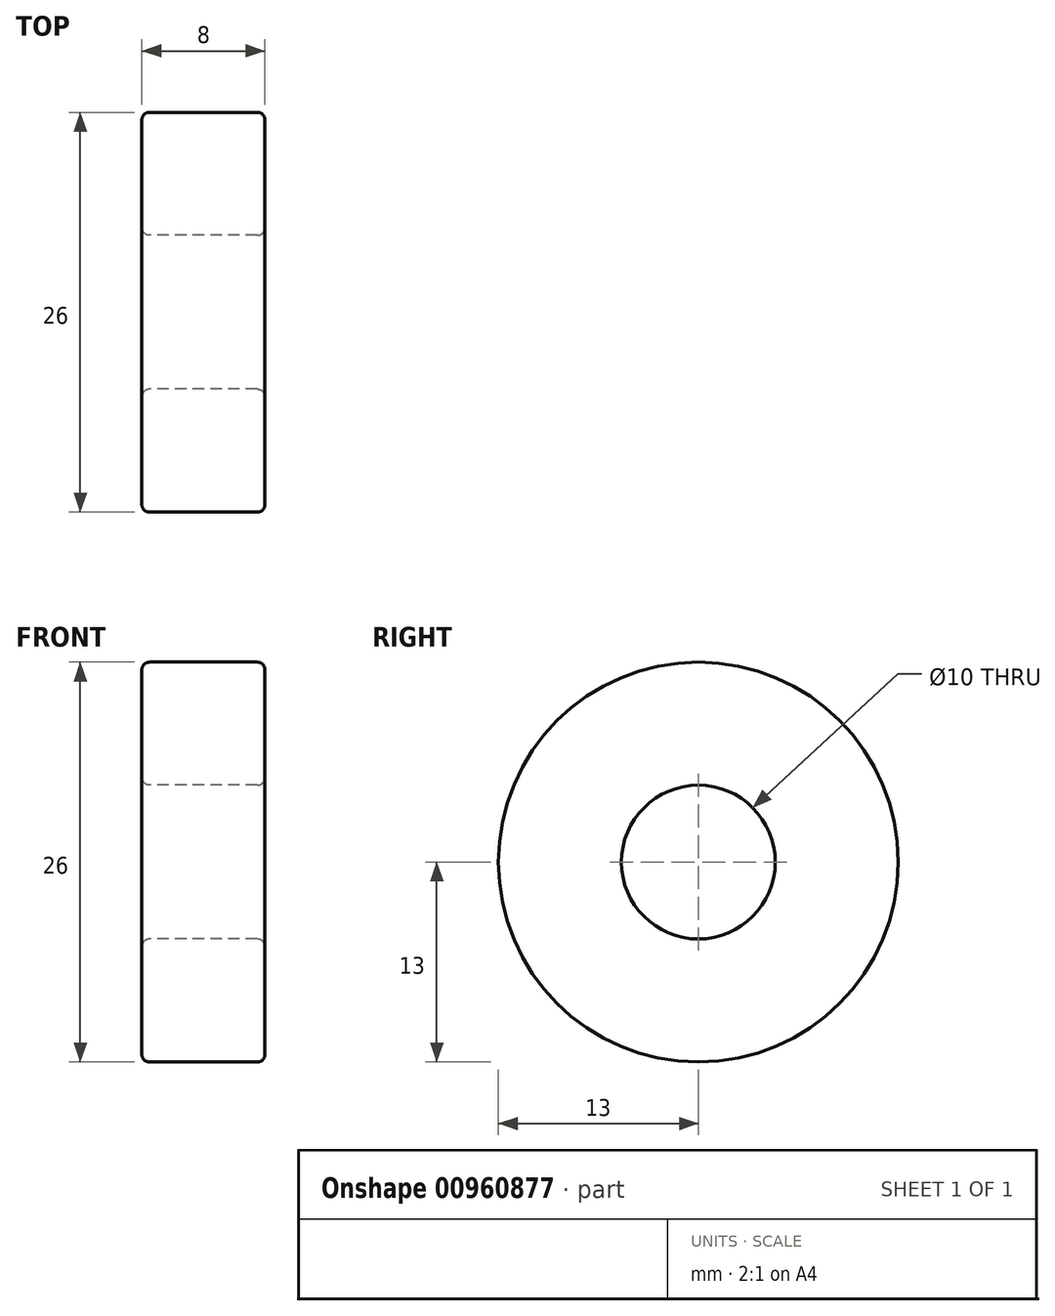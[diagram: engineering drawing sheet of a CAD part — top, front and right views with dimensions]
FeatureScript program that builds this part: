
annotation { "Feature Type Name" : "Feature", "Feature Type Description" : "" }
export const myFeature = defineFeature(function(context is Context, id is Id, definition is map)
    precondition{}
    {
        {
            var Q0;
            Q0=qCreatedBy(makeId("Front.planeOp"),FACE);
            var sketch = newSketch(context, id + "F0", { "sketchPlane" : qUnion([Q0])});
            skLineSegment(sketch, "E0.bottom", {"start": v(21.7, 13) * mm, "end": v(13.7, 13) * mm});
            skLineSegment(sketch, "E0.top", {"start": v(21.7, 5) * mm, "end": v(13.7, 5) * mm});
            skLineSegment(sketch, "E0.left", {"start": v(21.7, 13) * mm, "end": v(21.7, 5) * mm});
            skLineSegment(sketch, "E0.right", {"start": v(13.7, 13) * mm, "end": v(13.7, 5) * mm});
            skLineSegment(sketch, "E1", {"start": v(0, 0) * mm, "end": v(6.01, 0) * mm});
            skSolve(sketch);
        }
        {
            var Q0;
            Q0=makeQuery(id+"F0.imprint","IMPRINT",FACE,{"disambiguationData":[TD([[makeQuery(id+"F0.imprint","IMPRINT",EDGE,{"derivedFrom":sQuery(id+"F0.wireOp",EDGE,"E0.bottom")}),1.0]])]});
            var Q1;
            Q1=sQuery(id+"F0.wireOp",EDGE,"E1");
            revolve(context, id + "F1", {"surfaceOperationType" : NewSurfaceOperationType.NEW, "entities" : qUnion([Q0]), "axis" : qUnion([Q1]), "revolveType" : RevolveType.FULL});
        }
        {
            var Q0;
            Q0=makeQuery(id+"F1.opRevolve","SWEPT_EDGE",EDGE,{"disambiguationData":[OSD([sQuery(id+"F0.wireOp",EDGE,"E0.bottom"),sQuery(id+"F0.wireOp",EDGE,"E0.left")])]});
            var Q1;
            Q1=makeQuery(id+"F1.opRevolve","SWEPT_EDGE",EDGE,{"disambiguationData":[OSD([sQuery(id+"F0.wireOp",EDGE,"E0.bottom"),sQuery(id+"F0.wireOp",EDGE,"E0.right")])]});
            var Q2;
            Q2=makeQuery(id+"F1.opRevolve","SWEPT_EDGE",EDGE,{"disambiguationData":[OSD([sQuery(id+"F0.wireOp",EDGE,"E0.top"),sQuery(id+"F0.wireOp",EDGE,"E0.right")])]});
            var Q3;
            Q3=makeQuery(id+"F1.opRevolve","SWEPT_EDGE",EDGE,{"disambiguationData":[OSD([sQuery(id+"F0.wireOp",EDGE,"E0.top"),sQuery(id+"F0.wireOp",EDGE,"E0.left")])]});
            fillet(context, id + "F2", {"entities" : qUnion([Q0, Q1, Q2, Q3]), "radius" : 0.5 * mm, "tangentPropagation" : true, "allowEdgeOverflow" : false});
        }
    });
